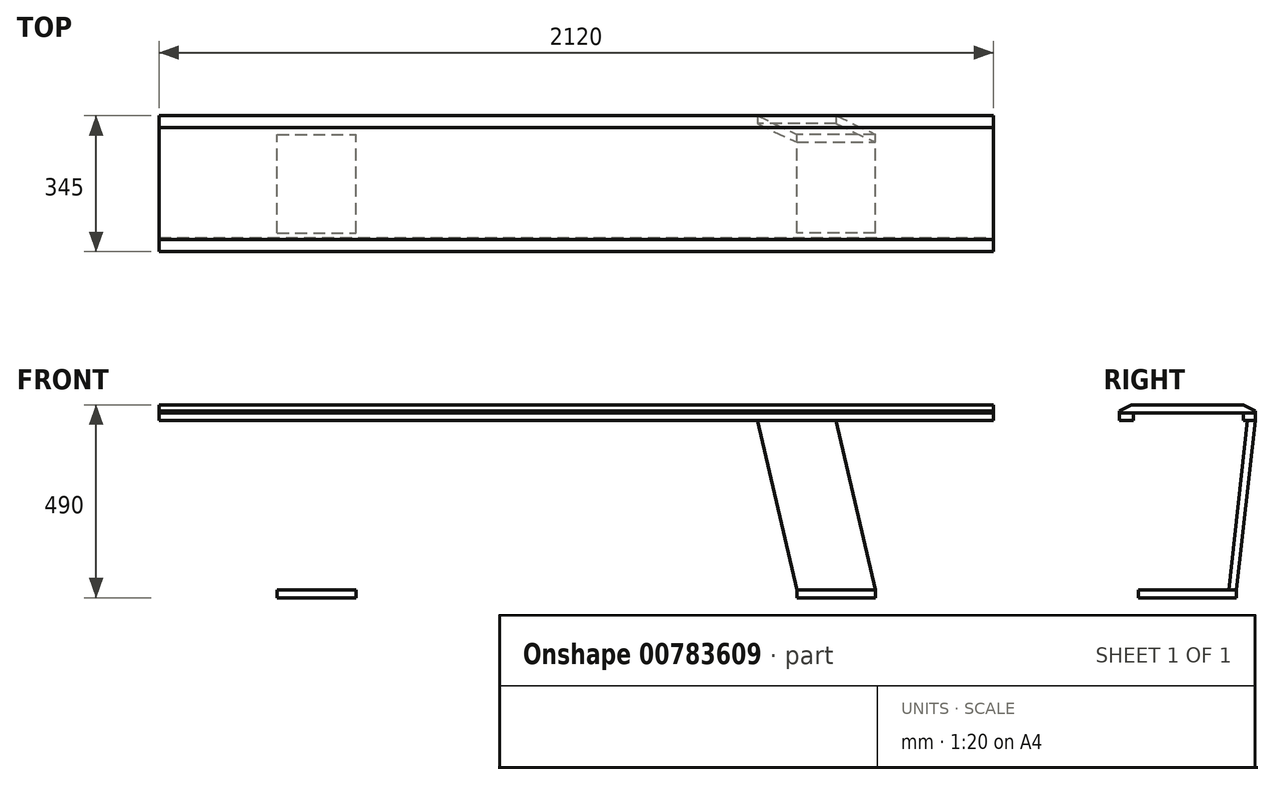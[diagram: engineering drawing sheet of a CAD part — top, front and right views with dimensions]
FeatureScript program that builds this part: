
annotation { "Feature Type Name" : "Feature", "Feature Type Description" : "" }
export const myFeature = defineFeature(function(context is Context, id is Id, definition is map)
    precondition{}
    {
        {
            var Q0;
            Q0=qCreatedBy(makeId("Top.planeOp"),FACE);
            var sketch = newSketch(context, id + "F0", { "sketchPlane" : qUnion([Q0])});
            skLineSegment(sketch, "E0.bottom", {"start": v(-1060, 172.5) * mm, "end": v(1060, 172.5) * mm});
            skLineSegment(sketch, "E0.top", {"start": v(-1060, -172.5) * mm, "end": v(1060, -172.5) * mm});
            skLineSegment(sketch, "E0.left", {"start": v(-1060, 172.5) * mm, "end": v(-1060, -172.5) * mm});
            skLineSegment(sketch, "E0.right", {"start": v(1060, 172.5) * mm, "end": v(1060, -172.5) * mm});
            skPoint(sketch, "E0.middle", {"position": v(0, 0) * mm});
            skSolve(sketch);
        }
        {
            var Q0;
            Q0=makeQuery(id+"F0.imprint","IMPRINT",FACE,{"disambiguationData":[TD([[makeQuery(id+"F0.imprint","IMPRINT",EDGE,{"derivedFrom":sQuery(id+"F0.wireOp",EDGE,"E0.bottom")}),-1.0]])]});
            extrude(context, id + "F1", {"entities" : qUnion([Q0]), "depth" : 20 * mm, "offsetDistance" : 25 * mm});
        }
        {
            var Q0;
            Q0=makeQuery(id+"F1.opExtrude","CAP_EDGE",EDGE,{"disambiguationData":[OSD([sQuery(id+"F0.wireOp",EDGE,"E0.top")])],"isStart":false});
            var Q1;
            Q1=makeQuery(id+"F1.opExtrude","CAP_EDGE",EDGE,{"disambiguationData":[OSD([sQuery(id+"F0.wireOp",EDGE,"E0.bottom")])],"isStart":false});
            chamfer(context, id + "F2", {"entities" : qUnion([Q0, Q1]), "chamferType" : ChamferType.TWO_OFFSETS, "width1" : 30 * mm, "oppositeDirection" : false, "width2" : 15 * mm, "tangentPropagation" : true});
        }
        {
            var Q0;
            Q0=makeQuery(id+"F1.opExtrude","CAP_FACE",FACE,{"disambiguationData":[OSD([sQuery(id+"F0.wireOp",EDGE,"E0.bottom"),sQuery(id+"F0.wireOp",EDGE,"E0.top"),sQuery(id+"F0.wireOp",EDGE,"E0.left"),sQuery(id+"F0.wireOp",EDGE,"E0.right")])],"isStart":true});
            var sketch = newSketch(context, id + "F3", { "sketchPlane" : qUnion([Q0])});
            skLineSegment(sketch, "E1.bottom", {"start": v(-1060, 172.5) * mm, "end": v(1060, 172.5) * mm});
            skLineSegment(sketch, "E1.top", {"start": v(-1060, 137.5) * mm, "end": v(1060, 137.5) * mm});
            skLineSegment(sketch, "E1.left", {"start": v(-1060, 172.5) * mm, "end": v(-1060, 137.5) * mm});
            skLineSegment(sketch, "E1.right", {"start": v(1060, 172.5) * mm, "end": v(1060, 137.5) * mm});
            skLineSegment(sketch, "E2.bottom", {"start": v(-1060, -172.5) * mm, "end": v(1060, -172.5) * mm});
            skLineSegment(sketch, "E2.top", {"start": v(-1060, -142.5) * mm, "end": v(1060, -142.5) * mm});
            skLineSegment(sketch, "E2.left", {"start": v(-1060, -172.5) * mm, "end": v(-1060, -142.5) * mm});
            skLineSegment(sketch, "E2.right", {"start": v(1060, -172.5) * mm, "end": v(1060, -142.5) * mm});
            skSolve(sketch);
        }
        {
            var Q0;
            Q0=makeQuery(id+"F3.imprint","IMPRINT",FACE,{"disambiguationData":[TD([[makeQuery(id+"F3.imprint","IMPRINT",EDGE,{"derivedFrom":sQuery(id+"F3.wireOp",EDGE,"E1.bottom")}),-1.0]])]});
            var Q1;
            Q1=makeQuery(id+"F3.imprint","IMPRINT",FACE,{"disambiguationData":[TD([[makeQuery(id+"F3.imprint","IMPRINT",EDGE,{"derivedFrom":sQuery(id+"F3.wireOp",EDGE,"E2.bottom")}),1.0]])]});
            extrude(context, id + "F4", {"entities" : qUnion([Q0, Q1]), "depth" : 20 * mm, "offsetDistance" : 25 * mm});
        }
        {
            var Q0;
            Q0=makeQuery(id+"F4.opExtrude","CAP_FACE",FACE,{"disambiguationData":[OSD([sQuery(id+"F3.wireOp",EDGE,"E1.bottom"),sQuery(id+"F3.wireOp",EDGE,"E1.top"),sQuery(id+"F3.wireOp",EDGE,"E1.left"),sQuery(id+"F3.wireOp",EDGE,"E1.right")])],"isStart":false});
            cPlane(context, id + "F5", {"entities" : qUnion([Q0]), "cplaneType" : CPlaneType.OFFSET, "offset" : 450 * mm, "width" : 150 * mm, "height" : 150 * mm});
        }
        {
            var Q0;
            Q0=qCreatedBy(makeId("Right.planeOp"),FACE);
            var sketch = newSketch(context, id + "F6", { "sketchPlane" : qUnion([Q0])});
            skLineSegment(sketch, "E3", {"start": v(172.5, -20) * mm, "end": v(133.13, -470) * mm});
            skLineSegment(sketch, "E4", {"start": v(133.13, -470) * mm, "end": v(-133.13, -470) * mm});
            skLineSegment(sketch, "E5", {"start": v(-133.13, -470) * mm, "end": v(-172.5, -20) * mm});
            skLineSegment(sketch, "E6", {"start": v(0, 0) * mm, "end": v(0, -470) * mm, "construction": true});
            skSolve(sketch);
        }
        {
            var Q0;
            Q0=makeQuery(id+"F4.opExtrude","CAP_FACE",FACE,{"disambiguationData":[OSD([sQuery(id+"F3.wireOp",EDGE,"E1.bottom"),sQuery(id+"F3.wireOp",EDGE,"E1.top"),sQuery(id+"F3.wireOp",EDGE,"E1.left"),sQuery(id+"F3.wireOp",EDGE,"E1.right")])],"isStart":false});
            var sketch = newSketch(context, id + "F7", { "sketchPlane" : qUnion([Q0])});
            skLineSegment(sketch, "E7.bottom", {"start": v(-860, 172.5) * mm, "end": v(-660, 172.5) * mm});
            skLineSegment(sketch, "E7.top", {"start": v(-860, 152.5) * mm, "end": v(-660, 152.5) * mm});
            skLineSegment(sketch, "E7.left", {"start": v(-860, 172.5) * mm, "end": v(-860, 152.5) * mm});
            skLineSegment(sketch, "E7.right", {"start": v(-660, 172.5) * mm, "end": v(-660, 152.5) * mm});
            skLineSegment(sketch, "E8.bottom", {"start": v(860, 172.5) * mm, "end": v(660, 172.5) * mm});
            skLineSegment(sketch, "E8.top", {"start": v(860, 152.5) * mm, "end": v(660, 152.5) * mm});
            skLineSegment(sketch, "E8.left", {"start": v(860, 172.5) * mm, "end": v(860, 152.5) * mm});
            skLineSegment(sketch, "E8.right", {"start": v(660, 172.5) * mm, "end": v(660, 152.5) * mm});
            skSolve(sketch);
        }
        {
            var Q0;
            Q0=makeQuery(id+"F4.opExtrude","CAP_FACE",FACE,{"disambiguationData":[OSD([sQuery(id+"F3.wireOp",EDGE,"E2.bottom"),sQuery(id+"F3.wireOp",EDGE,"E2.top"),sQuery(id+"F3.wireOp",EDGE,"E2.left"),sQuery(id+"F3.wireOp",EDGE,"E2.right")])],"isStart":false});
            var sketch = newSketch(context, id + "F8", { "sketchPlane" : qUnion([Q0])});
            skLineSegment(sketch, "E9.bottom", {"start": v(660, -172.5) * mm, "end": v(460, -172.5) * mm});
            skLineSegment(sketch, "E9.top", {"start": v(660, -152.5) * mm, "end": v(460, -152.5) * mm});
            skLineSegment(sketch, "E9.left", {"start": v(660, -172.5) * mm, "end": v(660, -152.5) * mm});
            skLineSegment(sketch, "E9.right", {"start": v(460, -172.5) * mm, "end": v(460, -152.5) * mm});
            skLineSegment(sketch, "E10.bottom", {"start": v(-660, -172.5) * mm, "end": v(-460, -172.5) * mm});
            skLineSegment(sketch, "E10.top", {"start": v(-660, -152.5) * mm, "end": v(-460, -152.5) * mm});
            skLineSegment(sketch, "E10.left", {"start": v(-660, -172.5) * mm, "end": v(-660, -152.5) * mm});
            skLineSegment(sketch, "E10.right", {"start": v(-460, -172.5) * mm, "end": v(-460, -152.5) * mm});
            skSolve(sketch);
        }
        {
            var Q0;
            Q0=qCreatedBy(id+"F5.planeOp",FACE);
            var sketch = newSketch(context, id + "F9", { "sketchPlane" : qUnion([Q0])});
            skLineSegment(sketch, "E11", {"start": v(-660, 0) * mm, "end": v(660, 0) * mm, "construction": true});
            skLineSegment(sketch, "E12.bottom", {"start": v(760, 125) * mm, "end": v(560, 125) * mm});
            skLineSegment(sketch, "E12.top", {"start": v(760, -125) * mm, "end": v(560, -125) * mm});
            skLineSegment(sketch, "E12.left", {"start": v(760, 125) * mm, "end": v(760, -125) * mm});
            skLineSegment(sketch, "E12.right", {"start": v(560, 125) * mm, "end": v(560, -125) * mm});
            skPoint(sketch, "E12.middle", {"position": v(660, 0) * mm});
            skLineSegment(sketch, "E13.bottom", {"start": v(-760, 125) * mm, "end": v(-560, 125) * mm});
            skLineSegment(sketch, "E13.top", {"start": v(-760, -125) * mm, "end": v(-560, -125) * mm});
            skLineSegment(sketch, "E13.left", {"start": v(-760, 125) * mm, "end": v(-760, -125) * mm});
            skLineSegment(sketch, "E13.right", {"start": v(-560, 125) * mm, "end": v(-560, -125) * mm});
            skPoint(sketch, "E13.middle", {"position": v(-660, 0) * mm});
            skSolve(sketch);
        }
        {
            var Q0;
            Q0=makeQuery(id+"F9.imprint","IMPRINT",FACE,{"disambiguationData":[TD([[makeQuery(id+"F9.imprint","IMPRINT",EDGE,{"derivedFrom":sQuery(id+"F9.wireOp",EDGE,"E12.bottom")}),1.0]])]});
            var Q1;
            Q1=makeQuery(id+"F9.imprint","IMPRINT",FACE,{"disambiguationData":[TD([[makeQuery(id+"F9.imprint","IMPRINT",EDGE,{"derivedFrom":sQuery(id+"F9.wireOp",EDGE,"E13.bottom")}),-1.0]])]});
            extrude(context, id + "F10", {"entities" : qUnion([Q0, Q1]), "oppositeDirection" : true, "depth" : 20 * mm, "offsetDistance" : 25 * mm});
        }
        {
            var Q0;
            Q0=qCreatedBy(makeId("Right.planeOp"),FACE);
            var sketch = newSketch(context, id + "F11", { "sketchPlane" : qUnion([Q0])});
            skLineSegment(sketch, "E14.0", {"start": v(172.5, 0) * mm, "end": v(-172.5, 0) * mm});
            skPoint(sketch, "E15.0", {"position": v(-162.5, -20) * mm});
            skLineSegment(sketch, "E16.0", {"start": v(-172.5, -20) * mm, "end": v(-152.5, -20) * mm});
            skSolve(sketch);
        }
        {
            var Q0;
            Q0=makeQuery(id+"F10.opExtrude","CAP_FACE",FACE,{"disambiguationData":[OSD([sQuery(id+"F9.wireOp",EDGE,"E12.bottom"),sQuery(id+"F9.wireOp",EDGE,"E12.top"),sQuery(id+"F9.wireOp",EDGE,"E12.left"),sQuery(id+"F9.wireOp",EDGE,"E12.right")])],"isStart":false});
            var sketch = newSketch(context, id + "F12", { "sketchPlane" : qUnion([Q0])});
            skLineSegment(sketch, "E17.bottom", {"start": v(560, 125) * mm, "end": v(760, 125) * mm});
            skLineSegment(sketch, "E17.top", {"start": v(560, 105) * mm, "end": v(760, 105) * mm});
            skLineSegment(sketch, "E17.left", {"start": v(560, 125) * mm, "end": v(560, 105) * mm});
            skLineSegment(sketch, "E17.right", {"start": v(760, 125) * mm, "end": v(760, 105) * mm});
            skLineSegment(sketch, "E18.bottom", {"start": v(760, -125) * mm, "end": v(560, -125) * mm});
            skLineSegment(sketch, "E18.top", {"start": v(760, -105) * mm, "end": v(560, -105) * mm});
            skLineSegment(sketch, "E18.left", {"start": v(760, -125) * mm, "end": v(760, -105) * mm});
            skLineSegment(sketch, "E18.right", {"start": v(560, -125) * mm, "end": v(560, -105) * mm});
            skSolve(sketch);
        }
        {
            var Q0;
            Q0=makeQuery(id+"F8.imprint","IMPRINT",FACE,{"disambiguationData":[TD([[makeQuery(id+"F8.imprint","IMPRINT",EDGE,{"derivedFrom":sQuery(id+"F8.wireOp",EDGE,"E9.bottom")}),1.0]])]});
            var Q1;
            Q1=makeQuery(id+"F12.imprint","IMPRINT",FACE,{"disambiguationData":[TD([[makeQuery(id+"F12.imprint","IMPRINT",EDGE,{"derivedFrom":sQuery(id+"F12.wireOp",EDGE,"E17.bottom")}),1.0]])]});
            loft(context, id + "F13", {"sheetProfilesArray" : [{ "sheetProfileEntities" : qUnion([Q0]) }, { "sheetProfileEntities" : qUnion([Q1]) }]});
        }
    });
